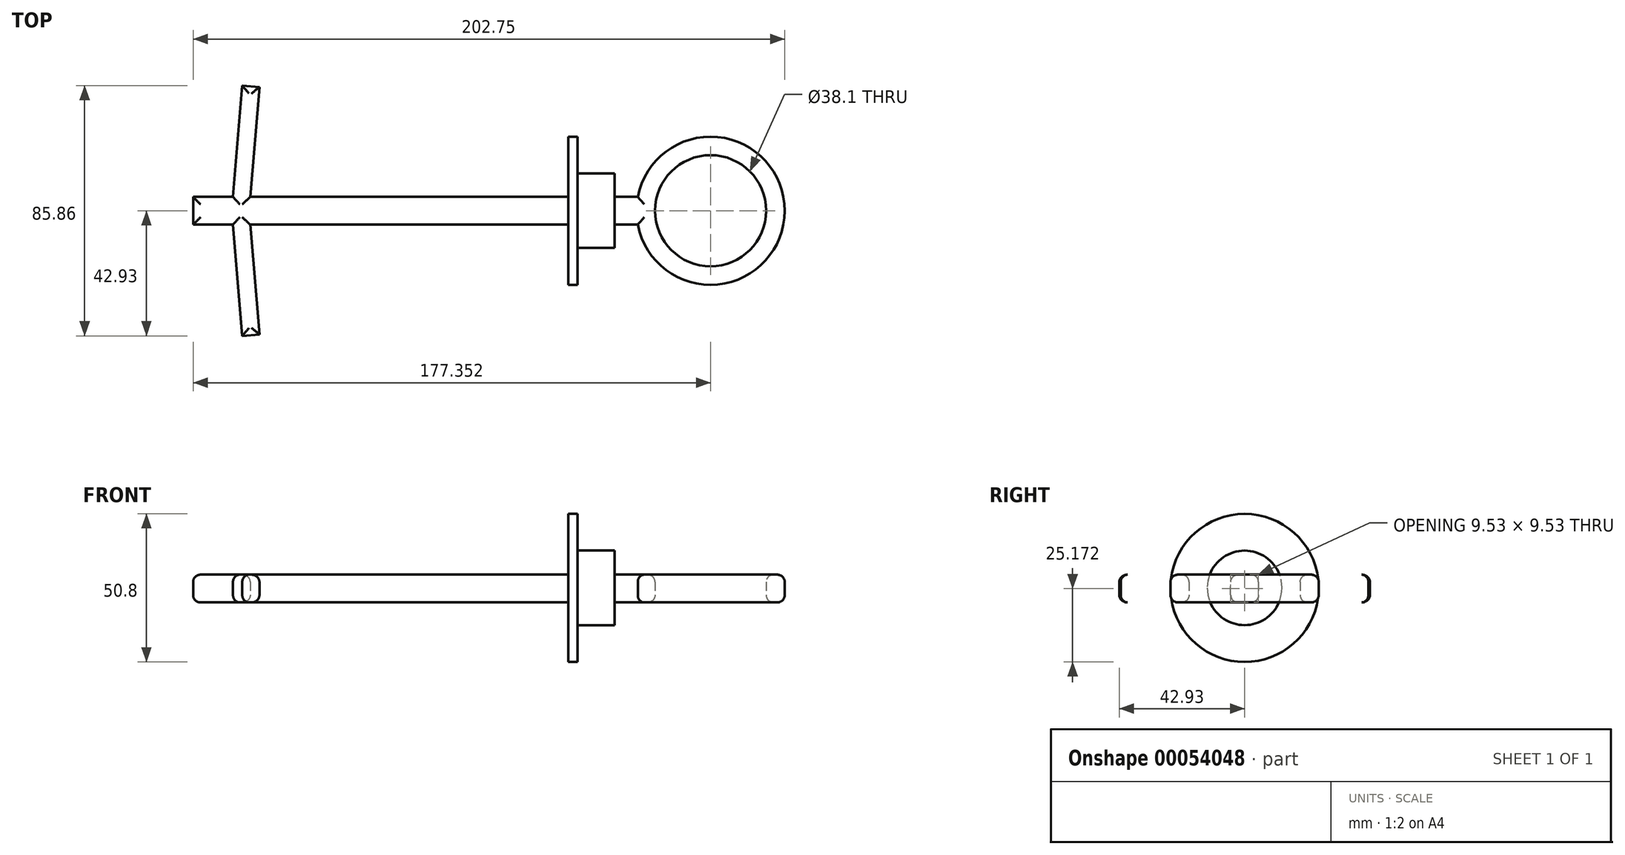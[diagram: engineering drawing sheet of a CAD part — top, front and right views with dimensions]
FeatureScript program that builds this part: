
annotation { "Feature Type Name" : "Feature", "Feature Type Description" : "" }
export const myFeature = defineFeature(function(context is Context, id is Id, definition is map)
    precondition{}
    {
        {
            var Q0;
            Q0=qCreatedBy(makeId("Top.planeOp"),FACE);
            var sketch = newSketch(context, id + "F0", { "sketchPlane" : qUnion([Q0])});
            skArc(sketch, "E0", {"start": v(49.27, -4.76) * mm, "mid": v(99.62, 0) * mm, "end": v(49.27, 4.76) * mm});
            skCircle(sketch, "E1", {"center": v(74.22, 0) * mm, "radius": 19.05 * mm});
            skLineSegment(sketch, "E2", {"start": v(49.27, 4.76) * mm, "end": v(-103.13, 4.76) * mm, "construction": true});
            skLineSegment(sketch, "E3", {"start": v(-103.13, 4.76) * mm, "end": v(-103.13, -4.76) * mm});
            skLineSegment(sketch, "E4", {"start": v(-103.13, -4.76) * mm, "end": v(49.27, -4.76) * mm, "construction": true});
            skLineSegment(sketch, "E5", {"start": v(74.22, 0) * mm, "end": v(-157.95, 0) * mm, "construction": true});
            skLineSegment(sketch, "E6", {"start": v(-103.13, 4.76) * mm, "end": v(-89.46, 4.76) * mm});
            skLineSegment(sketch, "E7", {"start": v(49.27, -4.76) * mm, "end": v(-83.52, -4.76) * mm});
            skLineSegment(sketch, "E8", {"start": v(-89.46, 4.76) * mm, "end": v(-86.29, 42.93) * mm});
            skLineSegment(sketch, "E9", {"start": v(-86.29, 42.93) * mm, "end": v(-80.38, 42.44) * mm});
            skLineSegment(sketch, "E10", {"start": v(-80.38, 42.44) * mm, "end": v(-83.52, 4.76) * mm});
            skLineSegment(sketch, "E11.MirrorCS", {"start": v(-86.29, -42.93) * mm, "end": v(-80.38, -42.44) * mm});
            skLineSegment(sketch, "E12.MirrorCS", {"start": v(-89.46, -4.76) * mm, "end": v(-86.29, -42.93) * mm});
            skLineSegment(sketch, "E13.MirrorCS", {"start": v(-80.38, -42.44) * mm, "end": v(-83.52, -4.76) * mm});
            skLineSegment(sketch, "E14.trimOffspring", {"start": v(-83.52, 4.76) * mm, "end": v(49.27, 4.76) * mm});
            skLineSegment(sketch, "E15.trimOffspring", {"start": v(-89.46, -4.76) * mm, "end": v(-103.13, -4.76) * mm});
            skSolve(sketch);
        }
        {
            var Q0;
            Q0=makeQuery(id+"F0.imprint","IMPRINT",FACE,{"disambiguationData":[TD([[makeQuery(id+"F0.imprint","IMPRINT",EDGE,{"derivedFrom":sQuery(id+"F0.wireOp",EDGE,"E0")}),1.0]])]});
            extrude(context, id + "F1", {"entities" : qUnion([Q0]), "depth" : 9.52 * mm});
        }
        {
            var Q0;
            Q0=makeQuery(id+"F1.opExtrude","CAP_FACE",FACE,{"disambiguationData":[OSD([sQuery(id+"F0.wireOp",EDGE,"E0"),sQuery(id+"F0.wireOp",EDGE,"E1"),sQuery(id+"F0.wireOp",EDGE,"E3"),sQuery(id+"F0.wireOp",EDGE,"E6"),sQuery(id+"F0.wireOp",EDGE,"E7"),sQuery(id+"F0.wireOp",EDGE,"E8"),sQuery(id+"F0.wireOp",EDGE,"E9"),sQuery(id+"F0.wireOp",EDGE,"E10"),sQuery(id+"F0.wireOp",EDGE,"E11.MirrorCS"),sQuery(id+"F0.wireOp",EDGE,"E12.MirrorCS"),sQuery(id+"F0.wireOp",EDGE,"E13.MirrorCS"),sQuery(id+"F0.wireOp",EDGE,"E14.trimOffspring"),sQuery(id+"F0.wireOp",EDGE,"E15.trimOffspring")])],"isStart":false});
            var Q1;
            Q1=makeQuery(id+"F1.opExtrude","CAP_FACE",FACE,{"disambiguationData":[OSD([sQuery(id+"F0.wireOp",EDGE,"E0"),sQuery(id+"F0.wireOp",EDGE,"E1"),sQuery(id+"F0.wireOp",EDGE,"E3"),sQuery(id+"F0.wireOp",EDGE,"E6"),sQuery(id+"F0.wireOp",EDGE,"E7"),sQuery(id+"F0.wireOp",EDGE,"E8"),sQuery(id+"F0.wireOp",EDGE,"E9"),sQuery(id+"F0.wireOp",EDGE,"E10"),sQuery(id+"F0.wireOp",EDGE,"E11.MirrorCS"),sQuery(id+"F0.wireOp",EDGE,"E12.MirrorCS"),sQuery(id+"F0.wireOp",EDGE,"E13.MirrorCS"),sQuery(id+"F0.wireOp",EDGE,"E14.trimOffspring"),sQuery(id+"F0.wireOp",EDGE,"E15.trimOffspring")])],"isStart":true});
            fillet(context, id + "F2", {"entities" : qUnion([Q0, Q1]), "radius" : 2.54 * mm, "tangentPropagation" : true, "allowEdgeOverflow" : false});
        }
        {
            var Q0;
            Q0=qCreatedBy(makeId("Right.planeOp"),FACE);
            cPlane(context, id + "F3", {"entities" : qUnion([Q0]), "cplaneType" : CPlaneType.OFFSET, "offset" : 25.4 * mm, "width" : 152.4 * mm, "height" : 152.4 * mm});
        }
        {
            var Q0;
            Q0=qCreatedBy(id+"F3.planeOp",FACE);
            var sketch = newSketch(context, id + "F4", { "sketchPlane" : qUnion([Q0])});
            skCircle(sketch, "E16", {"center": v(0, 4.99) * mm, "radius": 25.4 * mm});
            skCircle(sketch, "E17", {"center": v(0, 4.99) * mm, "radius": 16.27 * mm});
            skSolve(sketch);
        }
        {
            var Q0;
            Q0=makeQuery(id+"F4.imprint","IMPRINT",FACE,{"disambiguationData":[TD([[makeQuery(id+"F4.imprint","IMPRINT",EDGE,{"derivedFrom":sQuery(id+"F4.wireOp",EDGE,"E16")}),1.0]])]});
            var Q1;
            Q1=makeQuery(id+"F4.imprint","IMPRINT",FACE,{"disambiguationData":[TD([[makeQuery(id+"F4.imprint","IMPRINT",EDGE,{"derivedFrom":sQuery(id+"F4.wireOp",EDGE,"E17")}),1.0]])]});
            extrude(context, id + "F5", {"entities" : qUnion([Q0, Q1]), "operationType" : NewBodyOperationType.ADD, "depth" : 3.17 * mm});
        }
        {
            var Q0;
            Q0=makeQuery(id+"F5.opExtrude","CAP_FACE",FACE,{"disambiguationData":[OSD([sQuery(id+"F4.wireOp",EDGE,"E16")])],"isStart":false});
            var sketch = newSketch(context, id + "F6", { "sketchPlane" : qUnion([Q0])});
            skCircle(sketch, "E18", {"center": v(0, 4.99) * mm, "radius": 12.78 * mm});
            skSolve(sketch);
        }
        {
            var Q0;
            Q0=makeQuery(id+"F6.imprint","IMPRINT",FACE,{"disambiguationData":[TD([[makeQuery(id+"F6.imprint","IMPRINT",EDGE,{"derivedFrom":sQuery(id+"F6.wireOp",EDGE,"E18")}),1.0]])]});
            extrude(context, id + "F7", {"entities" : qUnion([Q0]), "operationType" : NewBodyOperationType.ADD, "depth" : 12.7 * mm});
        }
    });
